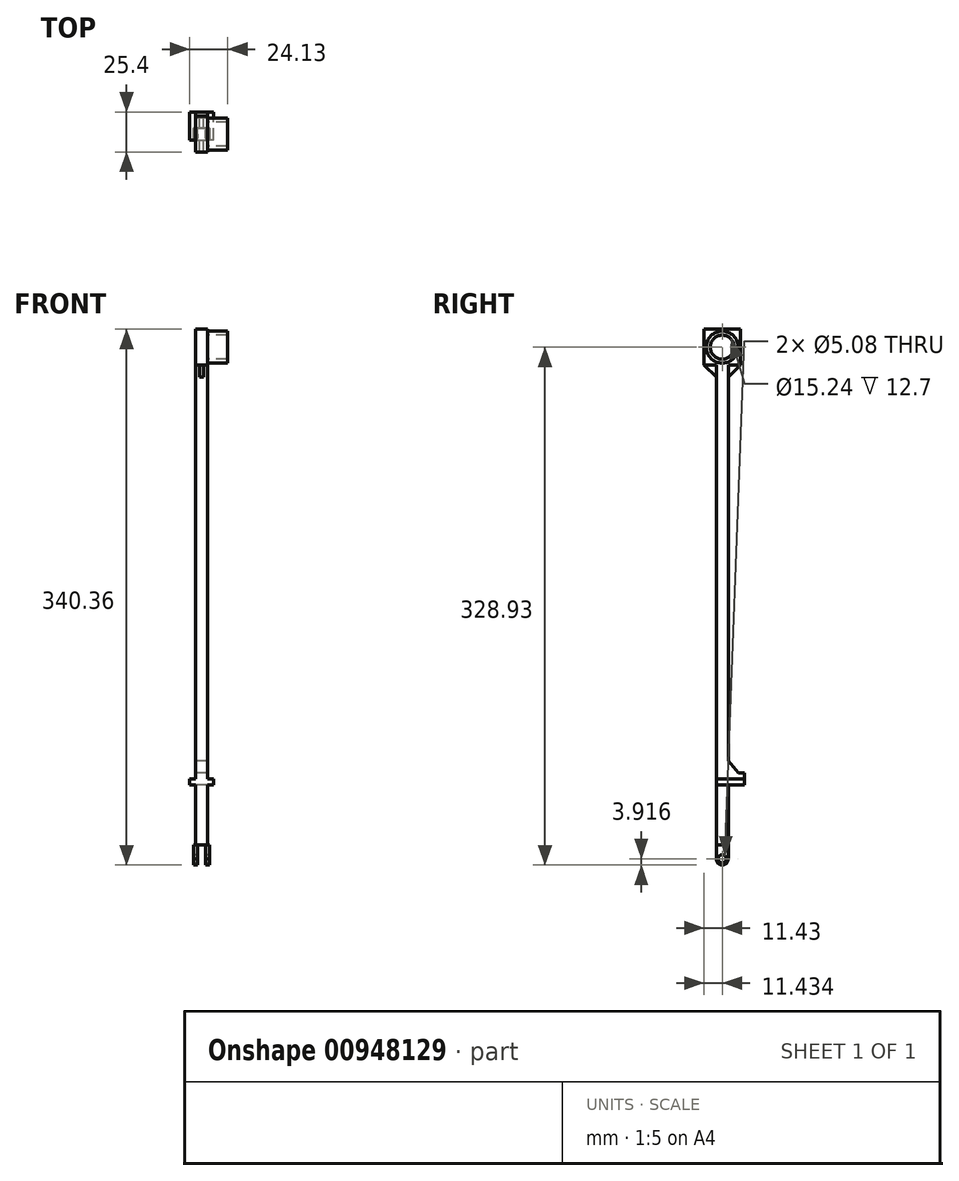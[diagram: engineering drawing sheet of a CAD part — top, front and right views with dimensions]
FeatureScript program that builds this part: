
annotation { "Feature Type Name" : "Feature", "Feature Type Description" : "" }
export const myFeature = defineFeature(function(context is Context, id is Id, definition is map)
    precondition{}
    {
        {
            var Q0;
            Q0=qCreatedBy(makeId("Top.planeOp"),FACE);
            var sketch = newSketch(context, id + "F0", { "sketchPlane" : qUnion([Q0])});
            skLineSegment(sketch, "E0.bottom", {"start": v(-35.84, -4.8) * mm, "end": v(-28.22, -4.8) * mm});
            skLineSegment(sketch, "E0.top", {"start": v(-35.84, -12.43) * mm, "end": v(-28.22, -12.43) * mm});
            skLineSegment(sketch, "E0.left", {"start": v(-35.84, -4.8) * mm, "end": v(-35.84, -12.43) * mm});
            skLineSegment(sketch, "E0.right", {"start": v(-28.22, -4.8) * mm, "end": v(-28.22, -12.43) * mm});
            skLineSegment(sketch, "E1.bottom", {"start": v(-29.49, -4.8) * mm, "end": v(-26.95, -4.8) * mm});
            skLineSegment(sketch, "E1.top", {"start": v(-29.49, -12.44) * mm, "end": v(-26.95, -12.44) * mm});
            skLineSegment(sketch, "E1.left", {"start": v(-29.49, -4.8) * mm, "end": v(-29.49, -12.44) * mm});
            skLineSegment(sketch, "E1.right", {"start": v(-26.95, -4.8) * mm, "end": v(-26.95, -12.44) * mm});
            skLineSegment(sketch, "E2", {"start": v(-26.95, -12.44) * mm, "end": v(-28.22, -12.43) * mm});
            skLineSegment(sketch, "E3", {"start": v(-29.49, -12.44) * mm, "end": v(-28.22, -12.43) * mm});
            skLineSegment(sketch, "E4", {"start": v(-29.49, -4.8) * mm, "end": v(-28.22, -4.8) * mm});
            skLineSegment(sketch, "E5.bottom", {"start": v(-34.57, -12.43) * mm, "end": v(-37.1, -12.43) * mm});
            skLineSegment(sketch, "E5.top", {"start": v(-34.57, -4.8) * mm, "end": v(-37.1, -4.8) * mm});
            skLineSegment(sketch, "E5.left", {"start": v(-34.57, -12.43) * mm, "end": v(-34.57, -4.8) * mm});
            skLineSegment(sketch, "E5.right", {"start": v(-37.1, -12.43) * mm, "end": v(-37.1, -4.8) * mm});
            skSolve(sketch);
        }
        {
            var Q0;
            Q0=makeQuery(id+"F0.imprint","IMPRINT",FACE,{"disambiguationData":[TD([[makeQuery(id+"F0.imprint","IMPRINT",EDGE,{"derivedFrom":sQuery(id+"F0.wireOp",EDGE,"E0.bottom")}),-1.0]])]});
            var Q1;
            {var subQ0=sQuery(id+"F0.wireOp",EDGE,"E0.right");Q1=makeQuery(id+"F0.imprint","IMPRINT",FACE,{"disambiguationData":[TD([[makeQuery(id+"F0.imprint","IMPRINT",EDGE,{"derivedFrom":subQ0}),-1.0]])]});}
            extrude(context, id + "F1", {"entities" : qUnion([Q0, Q1]), "depth" : 304.8 * mm, "offsetDistance" : 25.4 * mm});
        }
        {
            var Q0;
            Q0=makeQuery(id+"F0.imprint","IMPRINT",FACE,{"disambiguationData":[TD([[makeQuery(id+"F0.imprint","IMPRINT",EDGE,{"derivedFrom":sQuery(id+"F0.wireOp",EDGE,"E0.right")}),1.0]])]});
            var Q1;
            {var subQ0=sQuery(id+"F0.wireOp",EDGE,"E0.right");Q1=makeQuery(id+"F0.imprint","IMPRINT",FACE,{"disambiguationData":[TD([[makeQuery(id+"F0.imprint","IMPRINT",EDGE,{"derivedFrom":subQ0}),-1.0]])]});}
            var Q2;
            {var subQ0=sQuery(id+"F0.wireOp",EDGE,"E0.left");Q2=makeQuery(id+"F0.imprint","IMPRINT",FACE,{"disambiguationData":[TD([[makeQuery(id+"F0.imprint","IMPRINT",EDGE,{"derivedFrom":subQ0}),1.0]])]});}
            var Q3;
            {var subQ1=sQuery(id+"F0.wireOp",EDGE,"E0.left");Q3=makeQuery(id+"F0.imprint","IMPRINT",FACE,{"disambiguationData":[TD([[makeQuery(id+"F0.imprint","IMPRINT",EDGE,{"derivedFrom":subQ1}),-1.0]])]});}
            extrude(context, id + "F2", {"entities" : qUnion([Q0, Q1, Q2, Q3]), "operationType" : NewBodyOperationType.ADD, "oppositeDirection" : true, "depth" : 12.7 * mm, "offsetDistance" : 25.4 * mm});
        }
        {
            var Q0;
            Q0=makeQuery(id+"F2.opExtrude","SWEPT_FACE",FACE,{"disambiguationData":[OSD([sQuery(id+"F0.wireOp",EDGE,"E5.right")])]});
            var sketch = newSketch(context, id + "F3", { "sketchPlane" : qUnion([Q0])});
            skCircle(sketch, "E6", {"center": v(8.62, -8.78) * mm, "radius": 2.54 * mm});
            skPoint(sketch, "E6.centerSnap0", {"position": v(8.62, -12.7) * mm});
            skArc(sketch, "E7", {"start": v(8.62, -12.7) * mm, "mid": v(11.35, -11.55) * mm, "end": v(12.43, -8.78) * mm});
            skArc(sketch, "E8", {"start": v(4.8, -8.88) * mm, "mid": v(5.92, -11.58) * mm, "end": v(8.62, -12.7) * mm});
            skSolve(sketch);
        }
        {
            var Q0;
            {var subQ0=sQuery(id+"F3.wireOp",EDGE,"E7");var subQ1=sQuery(id+"F0.wireOp",EDGE,"E5.right");var subQ4=makeQuery(id+"F2.opExtrude","SWEPT_EDGE",EDGE,{"disambiguationData":[OSD([sQuery(id+"F0.wireOp",EDGE,"E5.bottom"),subQ1])]});var subQ5=makeQuery(id+"F3.imprint","INTERSECT",VERTEX,{"disambiguationData":[OD(1.0)],"derivedFrom":[subQ4,subQ0]});Q0=makeQuery(id+"F3.imprint","IMPRINT",FACE,{"disambiguationData":[TD([[makeQuery(id+"F3.imprint","IMPRINT",EDGE,{"disambiguationData":[TD([[subQ5,1.0]])],"derivedFrom":subQ0}),-1.0]])]});}
            var Q1;
            {var subQ0=sQuery(id+"F3.wireOp",EDGE,"E8");var subQ1=sQuery(id+"F0.wireOp",EDGE,"E5.right");var subQ2=makeQuery(id+"F2.opExtrude","CAP_EDGE",EDGE,{"disambiguationData":[OSD([subQ1])],"isStart":false});var subQ3=makeQuery(id+"F3.imprint","INTERSECT",VERTEX,{"derivedFrom":[subQ2,subQ0]});var subQ4=makeQuery(id+"F2.opExtrude","SWEPT_EDGE",EDGE,{"disambiguationData":[OSD([sQuery(id+"F0.wireOp",EDGE,"E5.top"),subQ1])]});var subQ5=makeQuery(id+"F3.imprint","INTERSECT",VERTEX,{"disambiguationData":[OD(1.0)],"derivedFrom":[subQ4,subQ0]});Q1=makeQuery(id+"F3.imprint","IMPRINT",FACE,{"disambiguationData":[TD([[makeQuery(id+"F3.imprint","IMPRINT",EDGE,{"disambiguationData":[TD([[subQ3,1.0],[subQ5,-1.0]])],"derivedFrom":subQ0}),-1.0]])]});}
            extrude(context, id + "F4", {"entities" : qUnion([Q0, Q1]), "operationType" : NewBodyOperationType.REMOVE, "oppositeDirection" : true, "depth" : 25.4 * mm, "offsetDistance" : 25.4 * mm});
        }
        {
            var Q0;
            Q0=makeQuery(id+"F3.imprint","IMPRINT",FACE,{"disambiguationData":[TD([[makeQuery(id+"F3.imprint","IMPRINT",EDGE,{"derivedFrom":sQuery(id+"F3.wireOp",EDGE,"E6")}),1.0]])]});
            extrude(context, id + "F5", {"entities" : qUnion([Q0]), "operationType" : NewBodyOperationType.REMOVE, "oppositeDirection" : true, "depth" : 25.4 * mm, "offsetDistance" : 25.4 * mm});
        }
        {
            var Q0;
            {var subQ0=sQuery(id+"F0.wireOp",EDGE,"E4");Q0=makeQuery(id+"F2.boolean.opBoolean","MERGE",FACE,{"derivedFrom":[makeQuery(id+"F1.opExtrude","SWEPT_FACE",FACE,{"disambiguationData":[OSD([sQuery(id+"F0.wireOp",EDGE,"E0.bottom"),subQ0])]}),makeQuery(id+"F2.opExtrude","SWEPT_FACE",FACE,{"disambiguationData":[OSD([sQuery(id+"F0.wireOp",EDGE,"E1.bottom"),subQ0])]})]});}
            var sketch = newSketch(context, id + "F6", { "sketchPlane" : qUnion([Q0])});
            skLineSegment(sketch, "E9.bottom", {"start": v(28.22, 38.1) * mm, "end": v(35.84, 38.1) * mm});
            skLineSegment(sketch, "E9.top", {"start": v(28.22, 45.72) * mm, "end": v(35.84, 45.72) * mm});
            skLineSegment(sketch, "E9.left", {"start": v(28.22, 38.1) * mm, "end": v(28.22, 45.72) * mm});
            skLineSegment(sketch, "E9.right", {"start": v(35.84, 38.1) * mm, "end": v(35.84, 45.72) * mm});
            skSolve(sketch);
        }
        {
            var Q0;
            Q0=makeQuery(id+"F6.imprint","IMPRINT",FACE,{"disambiguationData":[TD([[makeQuery(id+"F6.imprint","IMPRINT",EDGE,{"derivedFrom":sQuery(id+"F6.wireOp",EDGE,"E9.bottom")}),1.0]])]});
            extrude(context, id + "F7", {"entities" : qUnion([Q0]), "operationType" : NewBodyOperationType.ADD, "depth" : 10.16 * mm, "offsetDistance" : 25.4 * mm});
        }
        {
            var Q0;
            Q0=makeQuery(id+"F7.boolean.opBoolean","MERGE",FACE,{"derivedFrom":[makeQuery(id+"F1.opExtrude","SWEPT_FACE",FACE,{"disambiguationData":[OSD([sQuery(id+"F0.wireOp",EDGE,"E0.right")])]}),makeQuery(id+"F7.opExtrude","SWEPT_FACE",FACE,{"disambiguationData":[OSD([sQuery(id+"F6.wireOp",EDGE,"E9.left")])]})]});
            var sketch = newSketch(context, id + "F8", { "sketchPlane" : qUnion([Q0])});
            skLineSegment(sketch, "E10.bottom", {"start": v(-12.43, 38.1) * mm, "end": v(5.35, 38.1) * mm});
            skLineSegment(sketch, "E10.top", {"start": v(-12.43, 41.91) * mm, "end": v(5.35, 41.91) * mm});
            skLineSegment(sketch, "E10.left", {"start": v(-12.43, 38.1) * mm, "end": v(-12.43, 41.91) * mm});
            skLineSegment(sketch, "E10.right", {"start": v(5.35, 38.1) * mm, "end": v(5.35, 41.91) * mm});
            skSolve(sketch);
        }
        {
            var Q0;
            Q0=makeQuery(id+"F8.imprint","IMPRINT",FACE,{"disambiguationData":[TD([[makeQuery(id+"F8.imprint","IMPRINT",EDGE,{"derivedFrom":sQuery(id+"F8.wireOp",EDGE,"E10.top")}),-1.0]])]});
            extrude(context, id + "F9", {"entities" : qUnion([Q0]), "operationType" : NewBodyOperationType.ADD, "depth" : 3.8 * mm, "offsetDistance" : 25.4 * mm, "hasSecondDirection" : true, "secondDirectionOppositeDirection" : true, "secondDirectionDepth" : 11.43 * mm});
        }
        {
            var Q0;
            Q0=makeQuery(id+"F1.opExtrude","CAP_FACE",FACE,{"disambiguationData":[OSD([sQuery(id+"F0.wireOp",EDGE,"E0.bottom"),sQuery(id+"F0.wireOp",EDGE,"E0.top"),sQuery(id+"F0.wireOp",EDGE,"E0.left"),sQuery(id+"F0.wireOp",EDGE,"E0.right"),sQuery(id+"F0.wireOp",EDGE,"E4"),sQuery(id+"F0.wireOp",EDGE,"E5.bottom")])],"isStart":false});
            var sketch = newSketch(context, id + "F10", { "sketchPlane" : qUnion([Q0])});
            skPoint(sketch, "E11.middle", {"position": v(-32.03, -8.62) * mm});
            skPoint(sketch, "E11.middle.positionSnap0", {"position": v(-32.03, -12.43) * mm});
            skPoint(sketch, "E11.centerSnap0", {"position": v(-32.03, -12.43) * mm});
            skLineSegment(sketch, "E12.bottom", {"start": v(-28.22, 2.81) * mm, "end": v(-35.84, 2.81) * mm});
            skLineSegment(sketch, "E12.top", {"start": v(-28.22, -20.05) * mm, "end": v(-35.84, -20.05) * mm});
            skLineSegment(sketch, "E12.left", {"start": v(-28.22, 2.81) * mm, "end": v(-28.22, -20.05) * mm});
            skLineSegment(sketch, "E12.right", {"start": v(-35.84, 2.81) * mm, "end": v(-35.84, -20.05) * mm});
            skSolve(sketch);
        }
        {
            var Q0;
            {var subQ0=sQuery(id+"F10.wireOp",EDGE,"E12.top");Q0=makeQuery(id+"F10.imprint","IMPRINT",FACE,{"disambiguationData":[TD([[makeQuery(id+"F10.imprint","IMPRINT",EDGE,{"derivedFrom":subQ0}),-1.0]])]});}
            var Q1;
            {var subQ2=makeQuery(id+"F1.opExtrude","CAP_EDGE",EDGE,{"disambiguationData":[OSD([sQuery(id+"F0.wireOp",EDGE,"E0.bottom"),sQuery(id+"F0.wireOp",EDGE,"E4")])],"isStart":false});Q1=makeQuery(id+"F10.imprint","IMPRINT",FACE,{"disambiguationData":[TD([[makeQuery(id+"F10.imprint","IMPRINT",EDGE,{"derivedFrom":subQ2}),-1.0]])]});}
            var Q2;
            {var subQ0=sQuery(id+"F10.wireOp",EDGE,"E12.bottom");Q2=makeQuery(id+"F10.imprint","IMPRINT",FACE,{"disambiguationData":[TD([[makeQuery(id+"F10.imprint","IMPRINT",EDGE,{"derivedFrom":subQ0}),1.0]])]});}
            extrude(context, id + "F11", {"entities" : qUnion([Q0, Q1, Q2]), "operationType" : NewBodyOperationType.ADD, "depth" : 22.86 * mm, "offsetDistance" : 25.4 * mm});
        }
        {
            var Q0;
            {var subQ2=sQuery(id+"F0.wireOp",EDGE,"E0.right");var subQ5=sQuery(id+"F6.wireOp",EDGE,"E9.left");var subQ6=sQuery(id+"F6.wireOp",EDGE,"E9.top");Q0=makeQuery(id+"F11.boolean.opBoolean","MERGE",FACE,{"derivedFrom":[makeQuery(id+"F9.boolean.opBoolean","SPLIT",FACE,{"disambiguationData":[TD([makeQuery(id+"F7.opExtrude","SWEPT_FACE",FACE,{"disambiguationData":[OSD([subQ6])]})])],"derivedFrom":makeQuery(id+"F7.boolean.opBoolean","MERGE",FACE,{"derivedFrom":[makeQuery(id+"F1.opExtrude","SWEPT_FACE",FACE,{"disambiguationData":[OSD([subQ2])]}),makeQuery(id+"F7.opExtrude","SWEPT_FACE",FACE,{"disambiguationData":[OSD([subQ5])]})]})}),makeQuery(id+"F11.opExtrude","SWEPT_FACE",FACE,{"disambiguationData":[OSD([sQuery(id+"F10.wireOp",EDGE,"E12.left")])]})]});}
            var sketch = newSketch(context, id + "F12", { "sketchPlane" : qUnion([Q0])});
            skCircle(sketch, "E13", {"center": v(-8.62, 316.23) * mm, "radius": 7.62 * mm});
            skPoint(sketch, "E13.centerSnap0", {"position": v(-20.05, 316.23) * mm});
            skCircle(sketch, "E14", {"center": v(-8.62, 316.23) * mm, "radius": 10.16 * mm});
            skSolve(sketch);
        }
        {
            var Q0;
            Q0=makeQuery(id+"F12.imprint","IMPRINT",FACE,{"disambiguationData":[TD([[makeQuery(id+"F12.imprint","IMPRINT",EDGE,{"derivedFrom":sQuery(id+"F12.wireOp",EDGE,"E13")}),-1.0]])]});
            extrude(context, id + "F13", {"entities" : qUnion([Q0]), "operationType" : NewBodyOperationType.ADD, "depth" : 12.7 * mm, "offsetDistance" : 25.4 * mm});
        }
        {
            var Q0;
            {var subQ0=sQuery(id+"F10.wireOp",EDGE,"E12.top");var subQ2=sQuery(id+"F10.wireOp",EDGE,"E12.left");var subQ3=sQuery(id+"F0.wireOp",EDGE,"E0.top");var subQ4=sQuery(id+"F10.wireOp",EDGE,"E12.right");Q0=makeQuery(id+"F11.boolean.opBoolean","SPLIT",FACE,{"disambiguationData":[TD([makeQuery(id+"F2.opExtrude","SWEPT_FACE",FACE,{"disambiguationData":[OSD([subQ3])]})])],"derivedFrom":makeQuery(id+"F11.opExtrude","CAP_FACE",FACE,{"disambiguationData":[OSD([sQuery(id+"F10.wireOp",EDGE,"E12.bottom"),subQ0,subQ2,subQ4])],"isStart":true})});}
            var sketch = newSketch(context, id + "F14", { "sketchPlane" : qUnion([Q0])});
            skLineSegment(sketch, "E15.bottom", {"start": v(-33.3, 20.05) * mm, "end": v(-30.76, 20.05) * mm});
            skLineSegment(sketch, "E15.top", {"start": v(-33.3, 12.43) * mm, "end": v(-30.76, 12.43) * mm});
            skLineSegment(sketch, "E15.left", {"start": v(-33.3, 20.05) * mm, "end": v(-33.3, 12.43) * mm});
            skLineSegment(sketch, "E15.right", {"start": v(-30.76, 20.05) * mm, "end": v(-30.76, 12.43) * mm});
            skSolve(sketch);
        }
        {
            var Q0;
            Q0=makeQuery(id+"F14.imprint","IMPRINT",FACE,{"disambiguationData":[TD([[makeQuery(id+"F14.imprint","IMPRINT",EDGE,{"derivedFrom":sQuery(id+"F14.wireOp",EDGE,"E15.bottom")}),1.0]])]});
            extrude(context, id + "F15", {"entities" : qUnion([Q0]), "operationType" : NewBodyOperationType.ADD, "depth" : 7.62 * mm, "offsetDistance" : 25.4 * mm});
        }
        {
            var Q0;
            Q0=makeQuery(id+"F15.opExtrude","SWEPT_FACE",FACE,{"disambiguationData":[OSD([sQuery(id+"F14.wireOp",EDGE,"E15.left")])]});
            var sketch = newSketch(context, id + "F16", { "sketchPlane" : qUnion([Q0])});
            skLineSegment(sketch, "E16", {"start": v(20.05, 304.8) * mm, "end": v(12.43, 297.18) * mm});
            skSolve(sketch);
        }
        {
            var Q0;
            Q0=makeQuery(id+"F16.imprint","IMPRINT",FACE,{"disambiguationData":[TD([[makeQuery(id+"F16.imprint","IMPRINT",EDGE,{"derivedFrom":sQuery(id+"F16.wireOp",EDGE,"E16")}),1.0]])]});
            extrude(context, id + "F17", {"entities" : qUnion([Q0]), "operationType" : NewBodyOperationType.REMOVE, "oppositeDirection" : true, "depth" : 25.4 * mm, "offsetDistance" : 25.4 * mm});
        }
        {
            var Q0;
            {var subQ1=sQuery(id+"F10.wireOp",EDGE,"E12.right");var subQ2=sQuery(id+"F10.wireOp",EDGE,"E12.bottom");var subQ3=sQuery(id+"F10.wireOp",EDGE,"E12.left");Q0=makeQuery(id+"F11.boolean.opBoolean","SPLIT",FACE,{"disambiguationData":[TD([makeQuery(id+"F11.opExtrude","SWEPT_FACE",FACE,{"disambiguationData":[OSD([subQ2])]})])],"derivedFrom":makeQuery(id+"F11.opExtrude","CAP_FACE",FACE,{"disambiguationData":[OSD([subQ2,sQuery(id+"F10.wireOp",EDGE,"E12.top"),subQ3,subQ1])],"isStart":true})});}
            var sketch = newSketch(context, id + "F18", { "sketchPlane" : qUnion([Q0])});
            skLineSegment(sketch, "E17.bottom", {"start": v(-33.3, 4.8) * mm, "end": v(-30.76, 4.8) * mm});
            skLineSegment(sketch, "E17.top", {"start": v(-33.3, -2.81) * mm, "end": v(-30.76, -2.81) * mm});
            skLineSegment(sketch, "E17.left", {"start": v(-33.3, 4.8) * mm, "end": v(-33.3, -2.81) * mm});
            skLineSegment(sketch, "E17.right", {"start": v(-30.76, 4.8) * mm, "end": v(-30.76, -2.81) * mm});
            skSolve(sketch);
        }
        {
            var Q0;
            Q0=makeQuery(id+"F18.imprint","IMPRINT",FACE,{"disambiguationData":[TD([[makeQuery(id+"F18.imprint","IMPRINT",EDGE,{"derivedFrom":sQuery(id+"F18.wireOp",EDGE,"E17.bottom")}),-1.0]])]});
            extrude(context, id + "F19", {"entities" : qUnion([Q0]), "operationType" : NewBodyOperationType.ADD, "depth" : 7.62 * mm, "offsetDistance" : 25.4 * mm});
        }
        {
            var Q0;
            Q0=makeQuery(id+"F19.opExtrude","SWEPT_FACE",FACE,{"disambiguationData":[OSD([sQuery(id+"F18.wireOp",EDGE,"E17.left")])]});
            var sketch = newSketch(context, id + "F20", { "sketchPlane" : qUnion([Q0])});
            skLineSegment(sketch, "E18", {"start": v(-2.81, 304.8) * mm, "end": v(4.8, 297.18) * mm});
            skSolve(sketch);
        }
        {
            var Q0;
            Q0=makeQuery(id+"F20.imprint","IMPRINT",FACE,{"disambiguationData":[TD([[makeQuery(id+"F20.imprint","IMPRINT",EDGE,{"derivedFrom":sQuery(id+"F20.wireOp",EDGE,"E18")}),-1.0]])]});
            extrude(context, id + "F21", {"entities" : qUnion([Q0]), "operationType" : NewBodyOperationType.REMOVE, "oppositeDirection" : true, "depth" : 25.4 * mm, "offsetDistance" : 25.4 * mm});
        }
        {
            var Q0;
            Q0=makeQuery(id+"F7.opExtrude","SWEPT_FACE",FACE,{"disambiguationData":[OSD([sQuery(id+"F6.wireOp",EDGE,"E9.top")])]});
            var sketch = newSketch(context, id + "F22", { "sketchPlane" : qUnion([Q0])});
            skLineSegment(sketch, "E19.bottom", {"start": v(-28.22, -4.8) * mm, "end": v(-35.84, -4.8) * mm});
            skLineSegment(sketch, "E19.top", {"start": v(-28.22, 1.53) * mm, "end": v(-35.84, 1.53) * mm});
            skLineSegment(sketch, "E19.left", {"start": v(-28.22, -4.8) * mm, "end": v(-28.22, 1.53) * mm});
            skLineSegment(sketch, "E19.right", {"start": v(-35.84, -4.8) * mm, "end": v(-35.84, 1.53) * mm});
            skSolve(sketch);
        }
        {
            var Q0;
            Q0=makeQuery(id+"F22.imprint","IMPRINT",FACE,{"disambiguationData":[TD([[makeQuery(id+"F22.imprint","IMPRINT",EDGE,{"derivedFrom":sQuery(id+"F22.wireOp",EDGE,"E19.bottom")}),-1.0]])]});
            extrude(context, id + "F23", {"entities" : qUnion([Q0]), "operationType" : NewBodyOperationType.ADD, "depth" : 7.62 * mm, "offsetDistance" : 25.4 * mm});
        }
        {
            var Q0;
            {var subQ2=sQuery(id+"F0.wireOp",EDGE,"E0.left");var subQ5=sQuery(id+"F6.wireOp",EDGE,"E9.right");var subQ6=sQuery(id+"F6.wireOp",EDGE,"E9.top");Q0=makeQuery(id+"F23.boolean.opBoolean","MERGE",FACE,{"derivedFrom":[makeQuery(id+"F11.boolean.opBoolean","MERGE",FACE,{"derivedFrom":[makeQuery(id+"F9.boolean.opBoolean","SPLIT",FACE,{"disambiguationData":[TD([makeQuery(id+"F7.opExtrude","SWEPT_FACE",FACE,{"disambiguationData":[OSD([subQ6])]})])],"derivedFrom":makeQuery(id+"F7.boolean.opBoolean","MERGE",FACE,{"derivedFrom":[makeQuery(id+"F1.opExtrude","SWEPT_FACE",FACE,{"disambiguationData":[OSD([subQ2])]}),makeQuery(id+"F7.opExtrude","SWEPT_FACE",FACE,{"disambiguationData":[OSD([subQ5])]})]})}),makeQuery(id+"F11.opExtrude","SWEPT_FACE",FACE,{"disambiguationData":[OSD([sQuery(id+"F10.wireOp",EDGE,"E12.right")])]})]}),makeQuery(id+"F23.opExtrude","SWEPT_FACE",FACE,{"disambiguationData":[OSD([sQuery(id+"F22.wireOp",EDGE,"E19.right")])]})]});}
            var sketch = newSketch(context, id + "F24", { "sketchPlane" : qUnion([Q0])});
            skLineSegment(sketch, "E20", {"start": v(4.8, 53.34) * mm, "end": v(-1.53, 45.72) * mm});
            skSolve(sketch);
        }
        {
            var Q0;
            Q0=makeQuery(id+"F24.imprint","IMPRINT",FACE,{"disambiguationData":[TD([[makeQuery(id+"F24.imprint","IMPRINT",EDGE,{"derivedFrom":sQuery(id+"F24.wireOp",EDGE,"E20")}),-1.0]])]});
            extrude(context, id + "F25", {"entities" : qUnion([Q0]), "operationType" : NewBodyOperationType.REMOVE, "oppositeDirection" : true, "depth" : 25.4 * mm, "offsetDistance" : 25.4 * mm});
        }
    });
